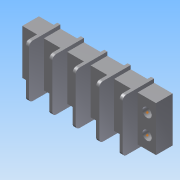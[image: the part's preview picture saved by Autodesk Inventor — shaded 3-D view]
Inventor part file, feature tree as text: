
AUTODESK INVENTOR PART (.ipt)
format: ipt  version: 2013 (Build 170138000, 138)  size: 208,384 bytes
history: native  units: in
note: dims shown in document units (in); Inventor stores cm internally (conversion verified against a paired STEP export)
features: sketch x12, extrude x4, plane x1, pattern_linear x1
ambient origin geometry x8: Origin, YZ Plane, XZ Plane, XY Plane, X Axis, Y Axis, Z Axis, Center Point
bodies: Solid1 (feature_tree)
feature tree (18):
  extrude  "Extrusion1"  Depth=0.73in
  extrude  "Extrusion2"  Depth=0.15in
  plane  "Work Plane1"
  extrude  "Extrusion3"  Depth=1.73in
  pattern_linear  "Rectangular Pattern1"  Count1=5 Spacing1=0.38in
  extrude  "Extrusion4"  Depth=0.21in
  sketch  "Sketch5"  dims[d9=-0.3in]
  sketch  "Sketch6"  dims[d10=0.06in]
  sketch  "Sketch7"  dims[d11=0.512in]
  sketch  "Sketch8"  dims[d12=0.0625in]
  sketch  "Sketch9"  dims[d13=0.05in d14=0.0in d15=1.9685in d17=0.38in]
  sketch  "Sketch10"  dims[d18=0.11in d19=0.21in]
  sketch  "Sketch11"  dims[d21=0.165in]
  sketch  "Sketch12"  dims[d26=1.5748in d28=0.38in d29=0.3937in d31=1.0in d33=0.125in d34=0.0in]
  sketch  "Sketch1"  dims[d0=2.17in d1=0.73in]
  sketch  "Sketch2"  dims[d2=0.27in d3=0.0in d4=0.15in]
  sketch  "Sketch3"  dims[d5=0.17in d6=1.73in]
  sketch  "Sketch4"  dims[d7=0.27in d8=0.0in]
